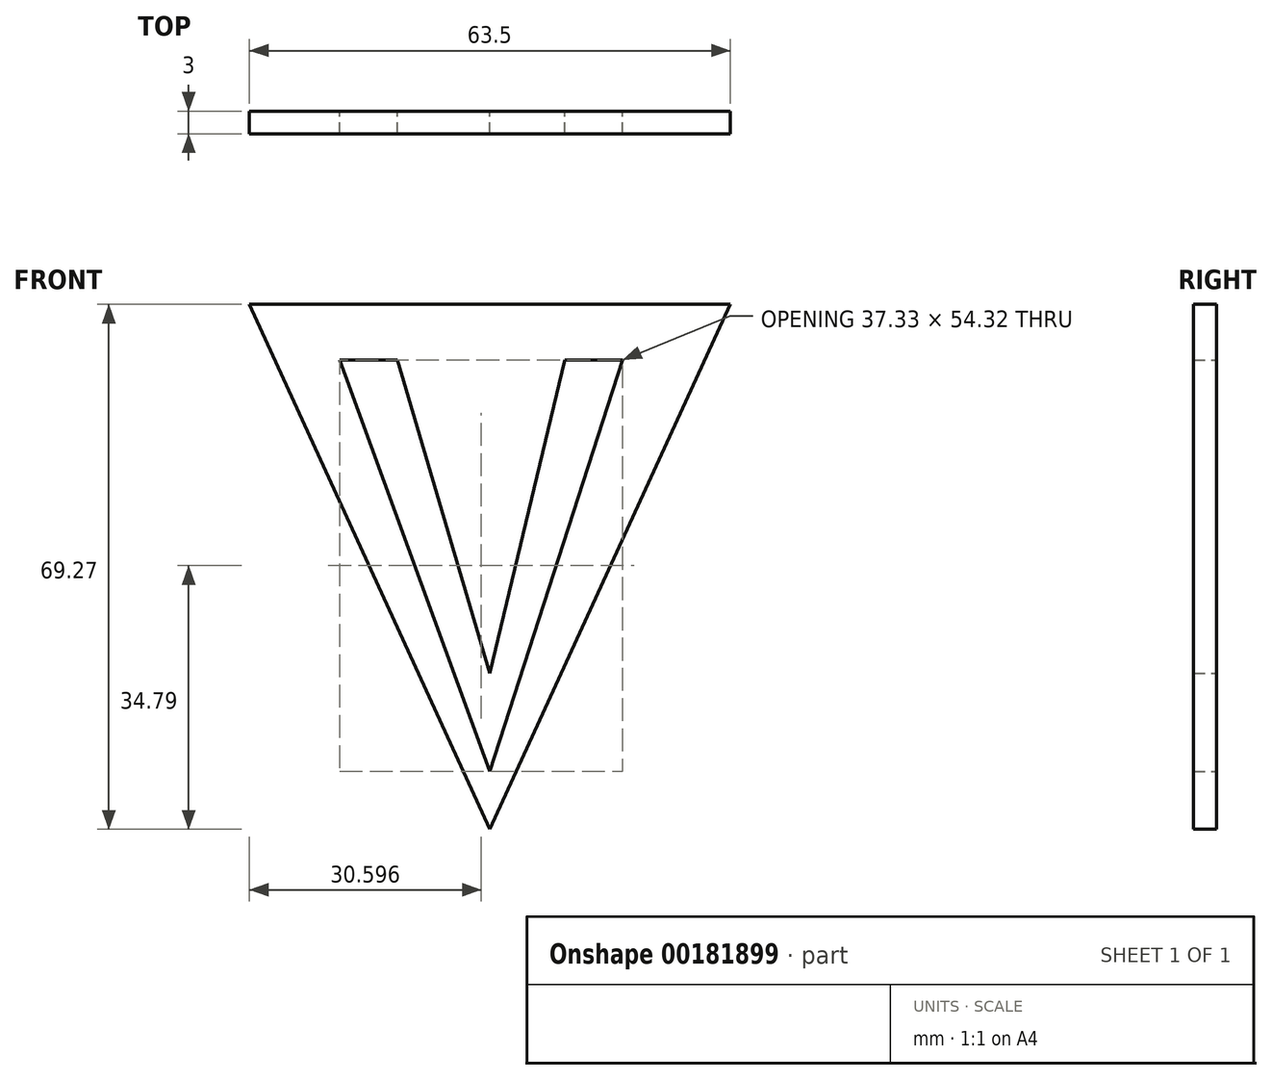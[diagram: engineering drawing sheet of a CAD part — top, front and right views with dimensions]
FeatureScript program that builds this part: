
annotation { "Feature Type Name" : "Feature", "Feature Type Description" : "" }
export const myFeature = defineFeature(function(context is Context, id is Id, definition is map)
    precondition{}
    {
        {
            var Q0;
            Q0=qCreatedBy(makeId("Front.planeOp"),FACE);
            var sketch = newSketch(context, id + "F0", { "sketchPlane" : qUnion([Q0])});
            skLineSegment(sketch, "E0", {"start": v(-31.75, 29.66) * mm, "end": v(0, -39.6) * mm});
            skLineSegment(sketch, "E1", {"start": v(-19.82, 22.34) * mm, "end": v(-12.2, 22.34) * mm});
            skLineSegment(sketch, "E2", {"start": v(-12.2, 22.34) * mm, "end": v(0, -19.04) * mm});
            skLineSegment(sketch, "E3", {"start": v(0, -19.04) * mm, "end": v(9.89, 22.34) * mm});
            skLineSegment(sketch, "E4", {"start": v(9.89, 22.34) * mm, "end": v(17.5, 22.34) * mm});
            skLineSegment(sketch, "E5", {"start": v(17.5, 22.34) * mm, "end": v(0, -31.98) * mm});
            skLineSegment(sketch, "E6", {"start": v(0, -31.98) * mm, "end": v(-19.82, 22.34) * mm});
            skLineSegment(sketch, "E7", {"start": v(0, -39.6) * mm, "end": v(31.75, 29.66) * mm});
            skLineSegment(sketch, "E8", {"start": v(-31.75, 29.66) * mm, "end": v(31.75, 29.66) * mm});
            skSolve(sketch);
        }
        {
            var Q0;
            Q0 = qSketchRegion(id + "F0", true);
            extrude(context, id + "F1", {"entities" : qUnion([Q0]), "depth" : 3 * mm});
        }
    });
